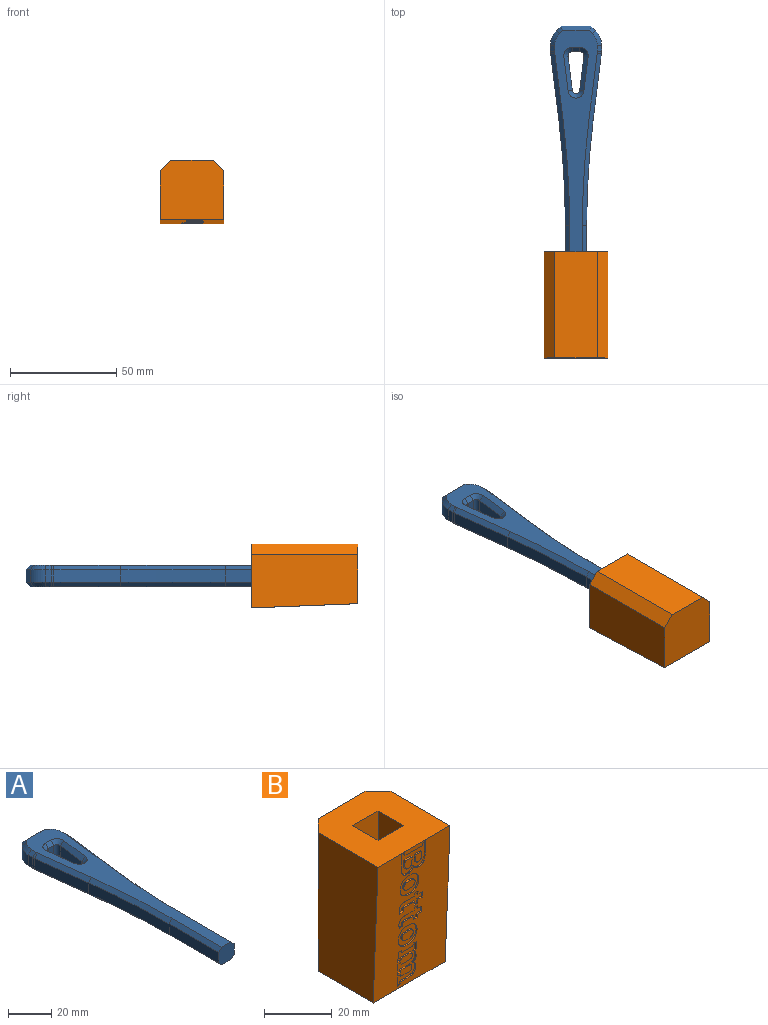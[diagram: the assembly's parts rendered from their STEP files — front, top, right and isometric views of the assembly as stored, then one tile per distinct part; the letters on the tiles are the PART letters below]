
ASSEMBLY  parts=2 mates=1
PART A: 69 faces, bbox 24x126x10 mm
  f0: plane 6x2.73mm, normal (1,0,0), area 16.4mm2, adj f22,f24,f43,f58
  f1: plane 14x6mm, normal (0,1,0), area 84mm2, adj f17,f18,f46,f61
  f2: plane 6x2.73mm, normal (-1,0,0), area 16.4mm2, adj f21,f23,f52,f66
  f3: plane 31.44x6mm, normal (-0.99,-0.12,0), area 190.1mm2, adj f19,f23,f51,f67
  f4: plane 32.3x6mm, normal (-1,0,0), area 193.8mm2, adj f5,f19,f47,f63
  f5: plane 10x10mm, normal (0,-1,0), area 92mm2, adj f4,f6,f11,f12,f39,f47,f54,f63
  f6: plane 32.3x6mm, normal (1,0,0), area 193.8mm2, adj f5,f20,f39,f54
  f7: plane 16x6mm, normal (0.99,0.12,0), area 96.7mm2, adj f14,f16,f29,f37
  f8: plane 6x3.47mm, normal (0,-1,0), area 20.8mm2, adj f13,f16,f25,f33
  f9: plane 16x6mm, normal (-0.99,0.12,0), area 96.7mm2, adj f13,f15,f28,f34
  f10: plane 31.44x6mm, normal (0.99,-0.12,0), area 190.1mm2, adj f20,f24,f41,f56
  f11: plane 124x20mm, normal (0,0,1), area 1077.7mm2, adj f5,f32,f33,f34,f35,f36,f37,f38
  f12: plane 124x20mm, normal (0,0,-1), area 1077.7mm2, adj f5,f25,f26,f27,f28,f29,f30,f31
  f13: cylinder r=2mm len=6mm, axis (0,0,-1), area 20.3mm2, adj f8,f9,f26,f32
  f14: cylinder r=2mm len=6mm, axis (0,0,1), area 15.9mm2, adj f7,f15,f31,f38
  f15: cylinder r=2mm len=6mm, axis (0,0,1), area 15.9mm2, adj f9,f14,f30,f36
  f16: cylinder r=2mm len=6mm, axis (0,0,-1), area 20.3mm2, adj f7,f8,f27,f35
  f17: plane 6x2.07mm, normal (0.71,0.71,0), area 17.6mm2, adj f1,f22,f45,f60
  f18: plane 6x2.07mm, normal (-0.71,0.71,0), area 17.6mm2, adj f1,f21,f48,f62
  f19: cylinder r=400mm len=49.15mm, axis (0,0,-1), area 295.6mm2, adj f3,f4,f49,f65
  f20: cylinder r=400mm len=49.15mm, axis (0,0,-1), area 295.6mm2, adj f6,f10,f40,f55
  f21: cylinder r=10mm len=7.07mm, axis (0,0,1), area 47.1mm2, adj f2,f18,f50,f64
  f22: cylinder r=10mm len=7.07mm, axis (0,0,-1), area 47.1mm2, adj f0,f17,f44,f59
  f23: cylinder r=10mm len=6mm, axis (0,0,-1), area 7.4mm2, adj f2,f3,f53,f68
  f24: cylinder r=10mm len=6mm, axis (0,0,-1), area 7.4mm2, adj f0,f10,f42,f57
  f25: plane 3.47x2mm, normal (0,-0.71,-0.71), area 9.8mm2, adj f8,f12,f26,f27
  f26: cone r=4mm half-angle=45deg, axis (0,0,-1), area 14.4mm2, adj f12,f13,f25,f28
  f27: cone r=4mm half-angle=45deg, axis (0,0,-1), area 14.4mm2, adj f12,f16,f25,f29
  f28: plane 16.25x3.97mm, normal (-0.7,0.09,-0.71), area 45.6mm2, adj f9,f12,f26,f30
  f29: plane 16.25x3.97mm, normal (0.7,0.09,-0.71), area 45.6mm2, adj f7,f12,f27,f31
  f30: cone r=4mm half-angle=45deg, axis (0,0,-1), area 11.5mm2, adj f12,f15,f28,f31
  f31: cone r=4mm half-angle=45deg, axis (0,0,-1), area 11.5mm2, adj f12,f14,f29,f30
  f32: cone r=4mm half-angle=45deg, axis (0,0,1), area 14.4mm2, adj f11,f13,f33,f34
  f33: plane 3.47x2mm, normal (0,-0.71,0.71), area 9.8mm2, adj f8,f11,f32,f35
  f34: plane 16.25x3.97mm, normal (-0.7,0.09,0.71), area 45.6mm2, adj f9,f11,f32,f36
  f35: cone r=4mm half-angle=45deg, axis (0,0,1), area 14.4mm2, adj f11,f16,f33,f37
  f36: cone r=4mm half-angle=45deg, axis (0,0,1), area 11.5mm2, adj f11,f15,f34,f38
  f37: plane 16.25x3.97mm, normal (0.7,0.09,0.71), area 45.6mm2, adj f7,f11,f35,f38
  f38: cone r=4mm half-angle=45deg, axis (0,0,1), area 11.5mm2, adj f11,f14,f36,f37
  f39: plane 32.3x2mm, normal (0.71,0,-0.71), area 91.4mm2, adj f5,f6,f12,f40
  f40: cone r=402mm half-angle=45deg, axis (0,0,-1), area 139.7mm2, adj f12,f20,f39,f41
  f41: plane 31.69x5.88mm, normal (0.7,-0.09,-0.71), area 89.6mm2, adj f10,f12,f40,f42
  f42: cone r=8mm half-angle=45deg, axis (0,0,1), area 3.1mm2, adj f12,f24,f41,f43
  f43: plane 2.73x2mm, normal (0.71,0,-0.71), area 7.7mm2, adj f0,f12,f42,f44
  f44: cone r=8mm half-angle=45deg, axis (0,0,1), area 20mm2, adj f12,f22,f43,f45
  f45: plane 3.49x2.9mm, normal (0.5,0.5,-0.71), area 7.1mm2, adj f12,f17,f44,f46
  f46: plane 14x2mm, normal (0,0.71,-0.71), area 37.3mm2, adj f1,f12,f45,f48
  f47: plane 32.3x2mm, normal (-0.71,0,-0.71), area 91.4mm2, adj f4,f5,f12,f49
  f48: plane 3.49x2.9mm, normal (-0.5,0.5,-0.71), area 7.1mm2, adj f12,f18,f46,f50
  f49: cone r=402mm half-angle=45deg, axis (0,0,-1), area 139.7mm2, adj f12,f19,f47,f51
  f50: cone r=8mm half-angle=45deg, axis (0,0,1), area 20mm2, adj f12,f21,f48,f52
  f51: plane 31.69x5.88mm, normal (-0.7,-0.09,-0.71), area 89.6mm2, adj f3,f12,f49,f53
  f52: plane 2.73x2mm, normal (-0.71,0,-0.71), area 7.7mm2, adj f2,f12,f50,f53
  f53: cone r=8mm half-angle=45deg, axis (0,0,1), area 3.1mm2, adj f12,f23,f51,f52
  f54: plane 32.3x2mm, normal (0.71,0,0.71), area 91.4mm2, adj f5,f6,f11,f55
  f55: cone r=402mm half-angle=45deg, axis (0,0,1), area 139.7mm2, adj f11,f20,f54,f56
  f56: plane 31.69x5.88mm, normal (0.7,-0.09,0.71), area 89.6mm2, adj f10,f11,f55,f57
  f57: cone r=8mm half-angle=45deg, axis (0,0,-1), area 3.1mm2, adj f11,f24,f56,f58
  f58: plane 2.73x2mm, normal (0.71,0,0.71), area 7.7mm2, adj f0,f11,f57,f59
  f59: cone r=8mm half-angle=45deg, axis (0,0,-1), area 20mm2, adj f11,f22,f58,f60
  f60: plane 3.49x2.9mm, normal (0.5,0.5,0.71), area 7.1mm2, adj f11,f17,f59,f61
  f61: plane 14x2mm, normal (0,0.71,0.71), area 37.3mm2, adj f1,f11,f60,f62
  f62: plane 3.49x2.9mm, normal (-0.5,0.5,0.71), area 7.1mm2, adj f11,f18,f61,f64
  f63: plane 32.3x2mm, normal (-0.71,0,0.71), area 91.4mm2, adj f4,f5,f11,f65
  f64: cone r=8mm half-angle=45deg, axis (0,0,-1), area 20mm2, adj f11,f21,f62,f66
  f65: cone r=402mm half-angle=45deg, axis (0,0,1), area 139.7mm2, adj f11,f19,f63,f67
  f66: plane 2.73x2mm, normal (-0.71,0,0.71), area 7.7mm2, adj f2,f11,f64,f68
  f67: plane 31.69x5.88mm, normal (-0.7,-0.09,0.71), area 89.6mm2, adj f3,f11,f65,f68
  f68: cone r=8mm half-angle=45deg, axis (0,0,-1), area 3.1mm2, adj f11,f23,f66,f67
PART B: 175 faces, bbox 30x30x50 mm
  f0: plane 50x30mm, normal (0,-1,-0.04), area 1230.9mm2, adj f2,f7,f8,f10,f11,f12,f13,f14
  f1: plane 50x20mm, normal (0,1,0), area 1000mm2, adj f8,f10,f173,f174
  f2: plane 50x25mm, normal (-1,0,0), area 1200mm2, adj f0,f8,f10,f173
  f3: plane 20x10.5mm, normal (1,0,0), area 210mm2, adj f4,f6,f8,f9
  f4: plane 20x10.5mm, normal (0,-1,0), area 210mm2, adj f3,f5,f8,f9
  f5: plane 20x10.5mm, normal (-1,0,0), area 210mm2, adj f4,f6,f8,f9
  f6: plane 20x10.5mm, normal (0,1,0), area 210mm2, adj f3,f5,f8,f9
  f7: plane 50x25mm, normal (1,0,0), area 1200mm2, adj f0,f8,f10,f174
  f8: plane 30x30mm, normal (0,0,1), area 764.7mm2, adj f0,f1,f2,f3,f4,f5,f6,f7
  f9: plane 10.5x10.5mm, normal (0,0,1), area 110.3mm2, adj f3,f4,f5,f6
  f10: plane 30x28mm, normal (0,0,-1), area 815mm2, adj f0,f1,f2,f7,f173,f174
  f11: plane 2.04x0.58mm, normal (-1,0,0), area 1mm2, adj f0,f12,f30,f31
  f12: plane 1.84x0.5mm, normal (0,0.04,-1), area 0.9mm2, adj f0,f11,f13,f31
  f13: plane 1.12x0.54mm, normal (-1,0,0), area 0.6mm2, adj f0,f12,f14,f31
  f14: plane 1.42x0.5mm, normal (0,0.04,-1), area 0.7mm2, adj f0,f13,f15,f31
  f15: plane 1.12x0.54mm, normal (1,0,0), area 0.6mm2, adj f0,f14,f16,f31
  f16: plane 3.84x0.5mm, normal (0,0.04,-1), area 1.9mm2, adj f0,f15,f17,f31
  f17: extruded ~1.83x0.59mm, area 1mm2, adj f0,f16,f18,f31
  f18: extruded ~1.64x0.58mm, area 0.9mm2, adj f0,f17,f19,f31
  f19: extruded ~0.74x0.53mm, area 0.4mm2, adj f0,f18,f20,f31
  f20: extruded ~0.69x0.53mm, area 0.3mm2, adj f0,f19,f21,f31
  f21: plane 1.47x0.51mm, normal (-0.12,-0.04,0.99), area 0.7mm2, adj f0,f20,f22,f31
  f22: extruded ~0.51x0.37mm, area 0.2mm2, adj f0,f21,f23,f31
  f23: extruded ~0.51x0.38mm, area 0.2mm2, adj f0,f22,f24,f31
  f24: extruded ~0.52x0.51mm, area 0.3mm2, adj f0,f23,f25,f31
  f25: extruded ~0.63x0.51mm, area 0.3mm2, adj f0,f24,f26,f31
  f26: plane 3.83x0.5mm, normal (0,-0.04,1), area 1.9mm2, adj f0,f25,f27,f31
  f27: plane 1.34x0.55mm, normal (1,0,0), area 0.7mm2, adj f0,f26,f28,f31
  f28: plane 1.42x0.5mm, normal (0,-0.04,1), area 0.7mm2, adj f0,f27,f29,f31
  f29: plane 1.34x0.55mm, normal (-1,0,0), area 0.7mm2, adj f0,f28,f30,f31
  f30: plane 1.84x0.5mm, normal (0,-0.04,1), area 0.9mm2, adj f0,f11,f29,f31
  f31: plane 9.51x4.68mm, normal (0,-1,-0.04), area 24.2mm2, adj f11,f12,f13,f14,f15,f16,f17,f18
  f32: plane 0.5x0.15mm, normal (0,0.04,-1), area 0.1mm2, adj f0,f33,f51,f52
  f33: extruded ~2.76x0.96mm, area 1.5mm2, adj f0,f32,f34,f52
  f34: extruded ~2.63x1.07mm, area 1.5mm2, adj f0,f33,f35,f52
  f35: extruded ~2.61x1.07mm, area 1.4mm2, adj f0,f34,f36,f52
  f36: extruded ~2.76x0.96mm, area 1.5mm2, adj f0,f35,f37,f52
  f37: plane 0.5x0.15mm, normal (0,-0.04,1), area 0.1mm2, adj f0,f36,f38,f52
  f38: extruded ~2.76x0.96mm, area 1.5mm2, adj f0,f37,f39,f52
  f39: extruded ~2.63x1.07mm, area 1.5mm2, adj f0,f38,f40,f52
  f40: extruded ~2.62x1.07mm, area 1.5mm2, adj f0,f39,f51,f52
  f41: plane 0.5x0.15mm, normal (0,-0.04,1), area 0.1mm2, adj f42,f50,f52,f53
  f42: extruded ~1.63x0.51mm, area 0.8mm2, adj f41,f43,f52,f53
  f43: extruded ~1.17x0.63mm, area 0.7mm2, adj f42,f44,f52,f53
  f44: extruded ~1.18x0.63mm, area 0.7mm2, adj f43,f45,f52,f53
  f45: extruded ~1.63x0.51mm, area 0.8mm2, adj f44,f46,f52,f53
  f46: plane 0.5x0.15mm, normal (0,0.04,-1), area 0.1mm2, adj f45,f47,f52,f53
  f47: extruded ~1.65x0.51mm, area 0.9mm2, adj f46,f48,f52,f53
  f48: extruded ~1.17x0.63mm, area 0.7mm2, adj f47,f49,f52,f53
  f49: extruded ~1.19x0.62mm, area 0.7mm2, adj f48,f50,f52,f53
  f50: extruded ~1.65x0.51mm, area 0.9mm2, adj f41,f49,f52,f53
  f51: extruded ~2.76x0.96mm, area 1.5mm2, adj f0,f32,f40,f52
  f52: plane 7.8x7.09mm, normal (0,-1,-0.04), area 33.2mm2, adj f32,f33,f34,f35,f36,f37,f38,f39
  f53: plane 4.69x3.04mm, normal (0,-1,-0.04), area 11.9mm2, adj f41,f42,f43,f44,f45,f46,f47,f48
  f54: plane 0.5x0.15mm, normal (0,0.04,-1), area 0.1mm2, adj f0,f55,f73,f74
  f55: extruded ~2.76x0.96mm, area 1.5mm2, adj f0,f54,f56,f74
  f56: extruded ~2.63x1.07mm, area 1.5mm2, adj f0,f55,f57,f74
  f57: extruded ~2.61x1.07mm, area 1.4mm2, adj f0,f56,f58,f74
  f58: extruded ~2.76x0.96mm, area 1.5mm2, adj f0,f57,f59,f74
  f59: plane 0.5x0.15mm, normal (0,-0.04,1), area 0.1mm2, adj f0,f58,f60,f74
  f60: extruded ~2.76x0.96mm, area 1.5mm2, adj f0,f59,f61,f74
  f61: extruded ~2.63x1.07mm, area 1.5mm2, adj f0,f60,f62,f74
  f62: extruded ~2.62x1.07mm, area 1.5mm2, adj f0,f61,f73,f74
  f63: plane 0.5x0.15mm, normal (0,-0.04,1), area 0.1mm2, adj f64,f72,f74,f75
  f64: extruded ~1.63x0.51mm, area 0.8mm2, adj f63,f65,f74,f75
  f65: extruded ~1.17x0.63mm, area 0.7mm2, adj f64,f66,f74,f75
  f66: extruded ~1.18x0.63mm, area 0.7mm2, adj f65,f67,f74,f75
  f67: extruded ~1.63x0.51mm, area 0.8mm2, adj f66,f68,f74,f75
  f68: plane 0.5x0.15mm, normal (0,0.04,-1), area 0.1mm2, adj f67,f69,f74,f75
  f69: extruded ~1.65x0.51mm, area 0.9mm2, adj f68,f70,f74,f75
  f70: extruded ~1.17x0.63mm, area 0.7mm2, adj f69,f71,f74,f75
  f71: extruded ~1.19x0.62mm, area 0.7mm2, adj f70,f72,f74,f75
  f72: extruded ~1.65x0.51mm, area 0.9mm2, adj f63,f71,f74,f75
  f73: extruded ~2.76x0.96mm, area 1.5mm2, adj f0,f54,f62,f74
  f74: plane 7.8x7.09mm, normal (0,-1,-0.04), area 33.2mm2, adj f54,f55,f56,f57,f58,f59,f60,f61
  f75: plane 4.69x3.04mm, normal (0,-1,-0.04), area 11.9mm2, adj f63,f64,f65,f66,f67,f68,f69,f70
  f76: plane 1.1x0.54mm, normal (0.98,0.01,-0.19), area 0.6mm2, adj f0,f77,f118,f119
  f77: plane 4.66x0.5mm, normal (0,0.04,-1), area 2.3mm2, adj f0,f76,f78,f119
  f78: plane 1x0.54mm, normal (-0.98,0.01,-0.21), area 0.5mm2, adj f0,f77,f79,f119
  f79: plane 1.22x0.5mm, normal (0,0.04,-1), area 0.6mm2, adj f0,f78,f80,f119
  f80: plane 3.89x0.65mm, normal (1,0,0), area 1.9mm2, adj f0,f79,f81,f119
  f81: plane 1.22x0.5mm, normal (0,-0.04,1), area 0.6mm2, adj f0,f80,f82,f119
  f82: plane 0.89x0.53mm, normal (-0.97,-0.01,0.23), area 0.4mm2, adj f0,f81,f83,f119
  f83: plane 4.06x0.5mm, normal (0,-0.04,1), area 2mm2, adj f0,f82,f84,f119
  f84: extruded ~0.53x0.52mm, area 0.3mm2, adj f0,f83,f85,f119
  f85: extruded ~0.74x0.53mm, area 0.4mm2, adj f0,f84,f86,f119
  f86: extruded ~0.85x0.53mm, area 0.5mm2, adj f0,f85,f87,f119
  f87: extruded ~1.18x0.51mm, area 0.6mm2, adj f0,f86,f88,f119
  f88: plane 3.13x0.5mm, normal (0,0.04,-1), area 1.6mm2, adj f0,f87,f89,f119
  f89: plane 0.84x0.53mm, normal (-0.97,0.01,-0.25), area 0.4mm2, adj f0,f88,f90,f119
  f90: plane 1.22x0.5mm, normal (0,0.04,-1), area 0.6mm2, adj f0,f89,f91,f119
  f91: plane 3.68x0.65mm, normal (1,0,0), area 1.8mm2, adj f0,f90,f92,f119
  f92: plane 1.22x0.5mm, normal (0,-0.04,1), area 0.6mm2, adj f0,f91,f93,f119
  f93: plane 0.84x0.53mm, normal (-0.97,-0.01,0.25), area 0.4mm2, adj f0,f92,f94,f119
  f94: plane 3.52x0.5mm, normal (0,-0.04,1), area 1.8mm2, adj f0,f93,f95,f119
  f95: extruded ~0.5x0.19mm, area 0.1mm2, adj f0,f94,f96,f119
  f96: extruded ~0.5x0.22mm, area 0.1mm2, adj f0,f95,f97,f119
  f97: extruded ~0.53x0.52mm, area 0.4mm2, adj f0,f96,f98,f119
  f98: extruded ~0.77x0.53mm, area 0.4mm2, adj f0,f97,f99,f119
  f99: extruded ~0.85x0.53mm, area 0.5mm2, adj f0,f98,f100,f119
  f100: extruded ~1.19x0.51mm, area 0.6mm2, adj f0,f99,f101,f119
  f101: plane 3.13x0.5mm, normal (0,0.04,-1), area 1.6mm2, adj f0,f100,f102,f119
  f102: plane 0.9x0.53mm, normal (-0.97,0.01,-0.23), area 0.5mm2, adj f0,f101,f103,f119
  f103: plane 1.22x0.5mm, normal (0,0.04,-1), area 0.6mm2, adj f0,f102,f104,f119
  f104: plane 3.9x0.66mm, normal (1,0,0), area 1.9mm2, adj f0,f103,f105,f119
  f105: plane 1.22x0.5mm, normal (0,-0.04,1), area 0.6mm2, adj f0,f104,f106,f119
  f106: plane 1x0.54mm, normal (-0.98,-0.01,0.21), area 0.5mm2, adj f0,f105,f107,f119
  f107: plane 3.13x0.5mm, normal (0,-0.04,1), area 1.6mm2, adj f0,f106,f108,f119
  f108: extruded ~2.34x0.66mm, area 1.2mm2, adj f0,f107,f109,f119
  f109: extruded ~1.77x0.77mm, area 1mm2, adj f0,f108,f110,f119
  f110: extruded ~1.33x0.55mm, area 0.7mm2, adj f0,f109,f111,f119
  f111: extruded ~0.95x0.92mm, area 0.7mm2, adj f0,f110,f112,f119
  f112: extruded ~0.97x0.8mm, area 0.6mm2, adj f0,f111,f113,f119
  f113: extruded ~1.26x0.55mm, area 0.6mm2, adj f0,f112,f114,f119
  f114: extruded ~1.28x0.55mm, area 0.7mm2, adj f0,f113,f115,f119
  f115: extruded ~0.93x0.84mm, area 0.6mm2, adj f0,f114,f116,f119
  f116: plane 0.99x0.5mm, normal (-0.08,-0.04,1), area 0.5mm2, adj f0,f115,f117,f119
  f117: plane 2.98x0.62mm, normal (-1,0,0), area 1.5mm2, adj f0,f116,f118,f119
  f118: plane 1.22x0.5mm, normal (0,0.04,-1), area 0.6mm2, adj f0,f76,f117,f119
  f119: plane 12.81x7.66mm, normal (0,-1,-0.04), area 59.6mm2, adj f76,f77,f78,f79,f80,f81,f82,f83
  f120: plane 2.04x0.58mm, normal (-1,0,0), area 1mm2, adj f0,f121,f139,f140
  f121: plane 1.84x0.5mm, normal (0,0.04,-1), area 0.9mm2, adj f0,f120,f122,f140
  f122: plane 1.12x0.54mm, normal (-1,0,0), area 0.6mm2, adj f0,f121,f123,f140
  f123: plane 1.42x0.5mm, normal (0,0.04,-1), area 0.7mm2, adj f0,f122,f124,f140
  f124: plane 1.12x0.54mm, normal (1,0,0), area 0.6mm2, adj f0,f123,f125,f140
  f125: plane 3.84x0.5mm, normal (0,0.04,-1), area 1.9mm2, adj f0,f124,f126,f140
  f126: extruded ~1.83x0.59mm, area 1mm2, adj f0,f125,f127,f140
  f127: extruded ~1.64x0.58mm, area 0.9mm2, adj f0,f126,f128,f140
  f128: extruded ~0.74x0.53mm, area 0.4mm2, adj f0,f127,f129,f140
  f129: extruded ~0.69x0.53mm, area 0.3mm2, adj f0,f128,f130,f140
  f130: plane 1.47x0.51mm, normal (-0.12,-0.04,0.99), area 0.7mm2, adj f0,f129,f131,f140
  f131: extruded ~0.51x0.37mm, area 0.2mm2, adj f0,f130,f132,f140
  f132: extruded ~0.51x0.38mm, area 0.2mm2, adj f0,f131,f133,f140
  f133: extruded ~0.52x0.51mm, area 0.3mm2, adj f0,f132,f134,f140
  f134: extruded ~0.63x0.51mm, area 0.3mm2, adj f0,f133,f135,f140
  f135: plane 3.83x0.5mm, normal (0,-0.04,1), area 1.9mm2, adj f0,f134,f136,f140
  f136: plane 1.34x0.55mm, normal (1,0,0), area 0.7mm2, adj f0,f135,f137,f140
  f137: plane 1.42x0.5mm, normal (0,-0.04,1), area 0.7mm2, adj f0,f136,f138,f140
  f138: plane 1.34x0.55mm, normal (-1,0,0), area 0.7mm2, adj f0,f137,f139,f140
  f139: plane 1.84x0.5mm, normal (0,-0.04,1), area 0.9mm2, adj f0,f120,f138,f140
  f140: plane 9.51x4.68mm, normal (0,-1,-0.04), area 24.2mm2, adj f120,f121,f122,f123,f124,f125,f126,f127
  f141: plane 4.51x0.68mm, normal (-1,0,0), area 2.2mm2, adj f0,f142,f169,f170
  f142: plane 1.22x0.5mm, normal (0,0.04,-1), area 0.6mm2, adj f0,f141,f143,f170
  f143: plane 1.1x0.54mm, normal (0.98,0.01,-0.19), area 0.5mm2, adj f0,f142,f144,f170
  f144: plane 7.26x0.5mm, normal (0,0.04,-1), area 3.6mm2, adj f0,f143,f145,f170
  f145: plane 1.1x0.54mm, normal (-0.98,0.01,-0.19), area 0.5mm2, adj f0,f144,f146,f170
  f146: plane 1.22x0.5mm, normal (0,0.04,-1), area 0.6mm2, adj f0,f145,f147,f170
  f147: plane 4.99x0.7mm, normal (1,0,0), area 2.5mm2, adj f0,f146,f148,f170
  f148: extruded ~2.73x0.75mm, area 1.4mm2, adj f0,f147,f149,f170
  f149: extruded ~2.2x0.98mm, area 1.2mm2, adj f0,f148,f150,f170
  f150: extruded ~1.48x0.52mm, area 0.8mm2, adj f0,f149,f151,f170
  f151: extruded ~1.38x0.84mm, area 0.8mm2, adj f0,f150,f152,f170
  f152: extruded ~1.1x0.83mm, area 0.7mm2, adj f0,f151,f153,f170
  f153: extruded ~1.25x0.51mm, area 0.7mm2, adj f0,f152,f154,f170
  f154: extruded ~2.08x1.02mm, area 1.2mm2, adj f0,f153,f169,f170
  f155: plane 2.04x0.58mm, normal (1,0,0), area 1mm2, adj f156,f167,f170,f172
  f156: extruded ~1.16x0.55mm, area 0.6mm2, adj f155,f157,f170,f172
  f157: extruded ~1.14x0.51mm, area 0.6mm2, adj f156,f158,f170,f172
  f158: extruded ~1.04x0.52mm, area 0.6mm2, adj f157,f159,f170,f172
  f159: extruded ~1.25x0.55mm, area 0.7mm2, adj f158,f160,f170,f172
  f160: plane 1.89x0.57mm, normal (-1,0,0), area 0.9mm2, adj f159,f167,f170,f172
  f161: plane 2.68x0.5mm, normal (0,-0.04,1), area 1.3mm2, adj f162,f168,f170,f171
  f162: plane 1.41x0.56mm, normal (1,0,0), area 0.7mm2, adj f161,f163,f170,f171
  f163: extruded ~1.34x0.55mm, area 0.7mm2, adj f162,f164,f170,f171
  f164: extruded ~1.04x0.52mm, area 0.6mm2, adj f163,f165,f170,f171
  f165: extruded ~0.97x0.52mm, area 0.6mm2, adj f164,f166,f170,f171
  f166: extruded ~1.27x0.55mm, area 0.7mm2, adj f165,f168,f170,f171
  f167: plane 2.92x0.5mm, normal (0,-0.04,1), area 1.5mm2, adj f155,f160,f170,f172
  f168: plane 1.48x0.56mm, normal (-1,0,0), area 0.7mm2, adj f161,f166,f170,f171
  f169: extruded ~2.8x0.7mm, area 1.5mm2, adj f0,f141,f154,f170
  f170: plane 10.12x8.65mm, normal (0,-1,-0.04), area 55mm2, adj f141,f142,f143,f144,f145,f146,f147,f148
  f171: plane 3.15x2.68mm, normal (0,-1,-0.04), area 7.6mm2, adj f161,f162,f163,f164,f165,f166,f168
  f172: plane 3.52x2.92mm, normal (0,-1,-0.04), area 9.5mm2, adj f155,f156,f157,f158,f159,f160,f167
  f173: plane 50x5mm, normal (-0.71,0.71,0), area 353.6mm2, adj f1,f2,f8,f10
  f174: plane 50x5mm, normal (0.71,0.71,0), area 353.6mm2, adj f1,f7,f8,f10
PLACE A t=(0,20,-5)mm
PLACE B rot(axis=(0,0.71,0.71),180deg) t=(0,0,0)mm
MATE fastened B.f9 <-> A.f5  axis (0,1,0) through (0,0,0)mm
